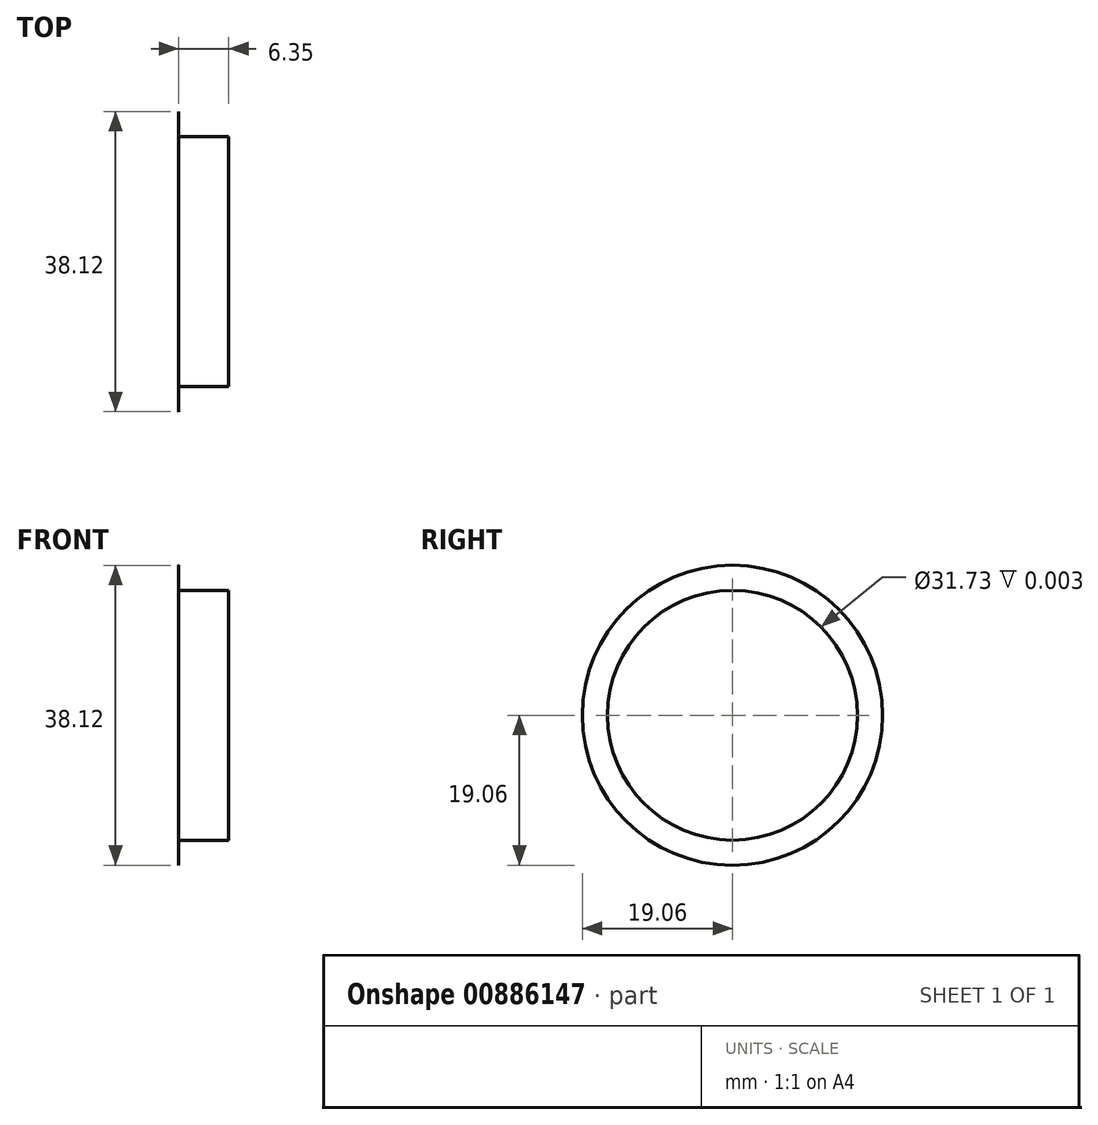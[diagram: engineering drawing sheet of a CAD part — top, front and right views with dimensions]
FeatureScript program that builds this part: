
annotation { "Feature Type Name" : "Feature", "Feature Type Description" : "" }
export const myFeature = defineFeature(function(context is Context, id is Id, definition is map)
    precondition{}
    {
        {
            var Q0;
            Q0=qCreatedBy(makeId("Right.planeOp"),FACE);
            var sketch = newSketch(context, id + "F0", { "sketchPlane" : qUnion([Q0])});
            skCircle(sketch, "E0", {"center": v(0, 0) * mm, "radius": 15.87 * mm});
            skSolve(sketch);
        }
        {
            var Q0;
            Q0=makeQuery(id+"F0.imprint","IMPRINT",FACE,{"disambiguationData":[TD([[makeQuery(id+"F0.imprint","IMPRINT",EDGE,{"derivedFrom":sQuery(id+"F0.wireOp",EDGE,"E0")}),1.0]])]});
            extrude(context, id + "F1", {"entities" : qUnion([Q0]), "depth" : 6.35 * mm, "offsetDistance" : 25.4 * mm});
        }
        {
            var Q0;
            Q0=makeQuery(id+"F1.opExtrude","CAP_FACE",FACE,{"disambiguationData":[OSD([sQuery(id+"F0.wireOp",EDGE,"E0")])],"isStart":true});
            var sketch = newSketch(context, id + "F2", { "sketchPlane" : qUnion([Q0])});
            skCircle(sketch, "E1", {"center": v(0, 0) * mm, "radius": 19.06 * mm});
            skSolve(sketch);
        }
        {
            var Q0;
            Q0=makeQuery(id+"F2.imprint","IMPRINT",FACE,{"disambiguationData":[TD([[makeQuery(id+"F2.imprint","IMPRINT",EDGE,{"derivedFrom":sQuery(id+"F2.wireOp",EDGE,"E1")}),1.0]])]});
            extrude(context, id + "F3", {"entities" : qUnion([Q0]), "depth" : 1 / 381 * mm, "offsetDistance" : 25.4 * mm});
        }
    });
